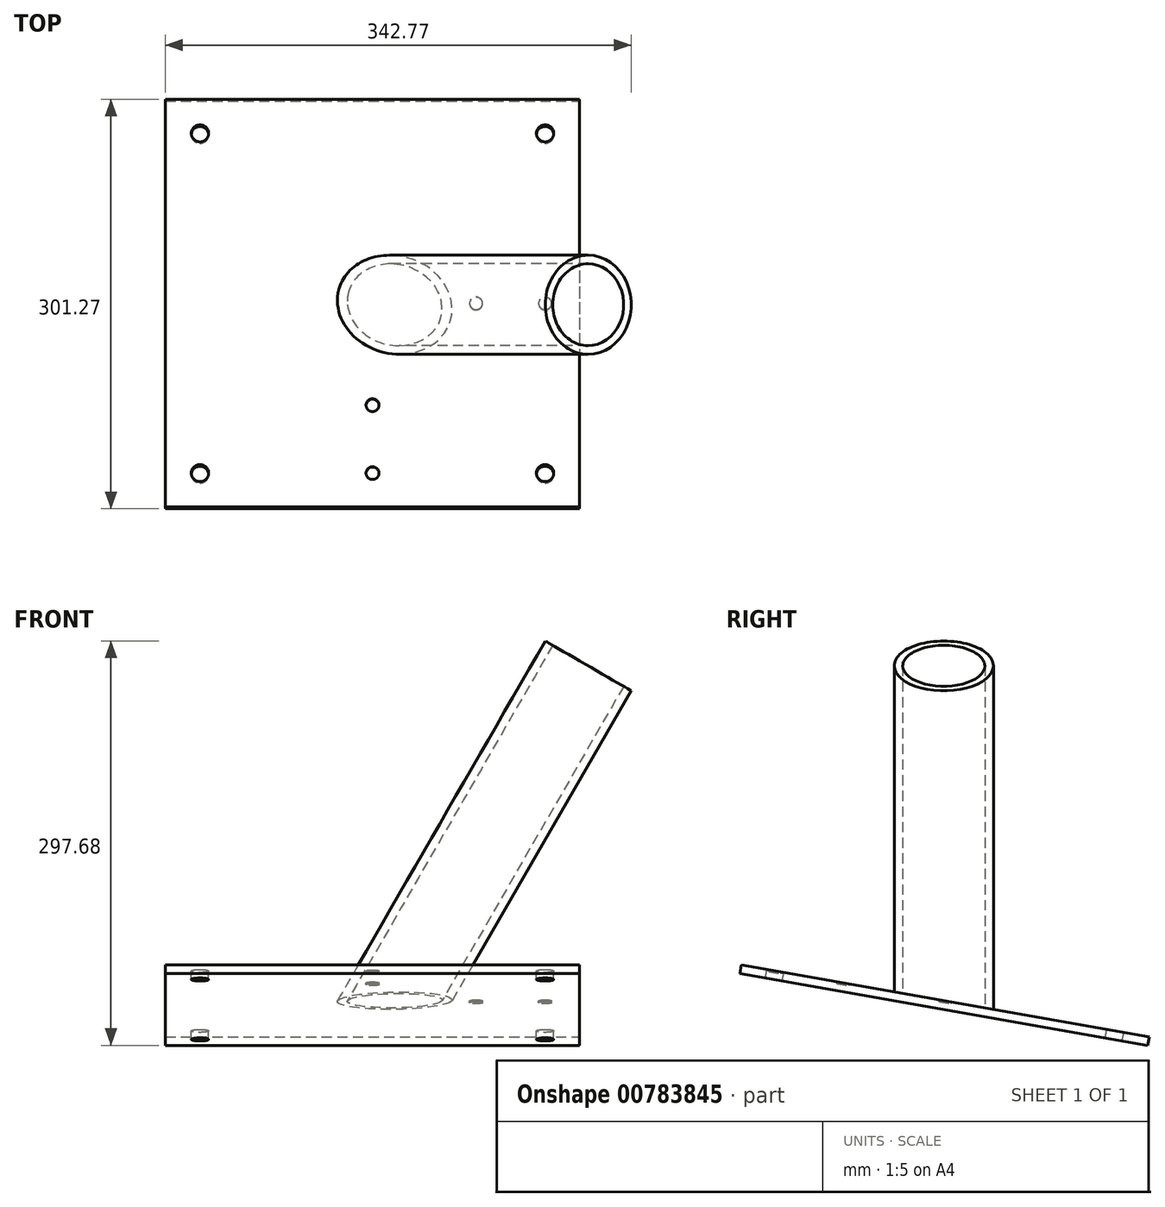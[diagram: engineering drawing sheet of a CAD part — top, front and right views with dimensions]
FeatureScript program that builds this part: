
annotation { "Feature Type Name" : "Feature", "Feature Type Description" : "" }
export const myFeature = defineFeature(function(context is Context, id is Id, definition is map)
    precondition{}
    {
        {
            var Q0;
            Q0=qCreatedBy(makeId("Top.planeOp"),FACE);
            var sketch = newSketch(context, id + "F0", { "sketchPlane" : qUnion([Q0])});
            skLineSegment(sketch, "E0.bottom", {"start": v(-25.4, 0) * mm, "end": v(0, 0) * mm});
            skLineSegment(sketch, "E0.top", {"start": v(-25.4, -25.4) * mm, "end": v(0, -25.4) * mm});
            skLineSegment(sketch, "E0.left", {"start": v(-25.4, 0) * mm, "end": v(-25.4, -25.4) * mm});
            skLineSegment(sketch, "E0.right", {"start": v(0, 0) * mm, "end": v(0, -25.4) * mm});
            skSolve(sketch);
        }
        {
            var Q0;
            Q0=sQuery(id+"F0.wireOp",EDGE,"E0.bottom");
            cPlane(context, id + "F1", {"entities" : qUnion([Q0]), "cplaneType" : CPlaneType.LINE_ANGLE, "offset" : 25.4 * mm, "angle" : 80 * degree, "width" : 152.4 * mm, "height" : 152.4 * mm});
        }
        {
            var Q0;
            Q0=qCreatedBy(id+"F1.planeOp",FACE);
            var sketch = newSketch(context, id + "F2", { "sketchPlane" : qUnion([Q0])});
            skLineSegment(sketch, "E1.bottom", {"start": v(-165.1, 152.4) * mm, "end": v(139.7, 152.4) * mm});
            skLineSegment(sketch, "E1.top", {"start": v(-165.1, -152.4) * mm, "end": v(139.7, -152.4) * mm});
            skLineSegment(sketch, "E1.left", {"start": v(-165.1, 152.4) * mm, "end": v(-165.1, -152.4) * mm});
            skLineSegment(sketch, "E1.right", {"start": v(139.7, 152.4) * mm, "end": v(139.7, -152.4) * mm});
            skSolve(sketch);
        }
        {
            var Q0;
            Q0=makeQuery(id+"F2.imprint","IMPRINT",FACE,{"disambiguationData":[TD([[makeQuery(id+"F2.imprint","IMPRINT",EDGE,{"derivedFrom":sQuery(id+"F2.wireOp",EDGE,"E1.bottom")}),-1.0]])]});
            extrude(context, id + "F3", {"entities" : qUnion([Q0]), "depth" : 6.35 * mm, "offsetDistance" : 25.4 * mm});
        }
        {
            var Q0;
            Q0=sQuery(id+"F0.wireOp",EDGE,"E0.right");
            cPlane(context, id + "F4", {"entities" : qUnion([Q0]), "cplaneType" : CPlaneType.LINE_ANGLE, "offset" : 25.4 * mm, "angle" : 330 * degree, "width" : 152.4 * mm, "height" : 152.4 * mm});
        }
        {
            var Q0;
            Q0=qCreatedBy(id+"F4.planeOp",FACE);
            var sketch = newSketch(context, id + "F5", { "sketchPlane" : qUnion([Q0])});
            skCircle(sketch, "E2", {"center": v(0, 0) * mm, "radius": 36.51 * mm});
            skCircle(sketch, "E3", {"center": v(0, 0) * mm, "radius": 30.16 * mm});
            skSolve(sketch);
        }
        {
            var Q0;
            Q0=makeQuery(id+"F5.imprint","IMPRINT",FACE,{"disambiguationData":[TD([[makeQuery(id+"F5.imprint","IMPRINT",EDGE,{"derivedFrom":sQuery(id+"F5.wireOp",EDGE,"E2")}),1.0]])]});
            extrude(context, id + "F6", {"entities" : qUnion([Q0]), "operationType" : NewBodyOperationType.ADD, "oppositeDirection" : true, "depth" : 292.1 * mm, "offsetDistance" : 25.4 * mm, "hasSecondDirection" : true, "secondDirectionOppositeDirection" : false, "secondDirectionDepth" : 15.24 * mm});
        }
        {
            var Q0;
            Q0=qCreatedBy(makeId("Right.planeOp"),FACE);
            var sketch = newSketch(context, id + "F7", { "sketchPlane" : qUnion([Q0])});
            skLineSegment(sketch, "E4", {"start": v(47.01, -8.29) * mm, "end": v(-49, 8.64) * mm});
            skLineSegment(sketch, "E5", {"start": v(-49, 8.64) * mm, "end": v(-49, -36.62) * mm});
            skLineSegment(sketch, "E6", {"start": v(-49, -36.62) * mm, "end": v(47.01, -36.62) * mm});
            skLineSegment(sketch, "E7", {"start": v(47.01, -36.62) * mm, "end": v(47.01, -8.29) * mm});
            skSolve(sketch);
        }
        {
            var Q0;
            Q0=makeQuery(id+"F7.imprint","IMPRINT",FACE,{"disambiguationData":[TD([[makeQuery(id+"F7.imprint","IMPRINT",EDGE,{"derivedFrom":sQuery(id+"F7.wireOp",EDGE,"E4")}),1.0]])]});
            extrude(context, id + "F8", {"entities" : qUnion([Q0]), "operationType" : NewBodyOperationType.REMOVE, "oppositeDirection" : true, "depth" : 50.8 * mm, "offsetDistance" : 25.4 * mm, "hasSecondDirection" : true, "secondDirectionOppositeDirection" : false, "secondDirectionDepth" : 50.8 * mm});
        }
        {
            var Q0;
            {var subQ0=sQuery(id+"F2.wireOp",EDGE,"E1.left");var subQ1=sQuery(id+"F2.wireOp",EDGE,"E1.top");var subQ2=sQuery(id+"F2.wireOp",EDGE,"E1.right");var subQ3=sQuery(id+"F2.wireOp",EDGE,"E1.bottom");Q0=makeQuery(id+"F6.boolean.opBoolean","SPLIT",FACE,{"disambiguationData":[TD([makeQuery(id+"F3.opExtrude","SWEPT_FACE",FACE,{"disambiguationData":[OSD([subQ3])]})])],"derivedFrom":makeQuery(id+"F3.opExtrude","CAP_FACE",FACE,{"disambiguationData":[OSD([subQ3,subQ1,subQ0,subQ2])],"isStart":false})});}
            var sketch = newSketch(context, id + "F9", { "sketchPlane" : qUnion([Q0])});
            skCircle(sketch, "E8", {"center": v(-12.7, -76.2) * mm, "radius": 4.76 * mm});
            skCircle(sketch, "E9", {"center": v(114.3, 0) * mm, "radius": 4.76 * mm});
            skCircle(sketch, "E10", {"center": v(63.5, 0) * mm, "radius": 4.76 * mm});
            skCircle(sketch, "E11", {"center": v(-12.7, -127) * mm, "radius": 4.76 * mm});
            skSolve(sketch);
        }
        {
            var Q0;
            Q0=makeQuery(id+"F9.imprint","IMPRINT",FACE,{"disambiguationData":[TD([[makeQuery(id+"F9.imprint","IMPRINT",EDGE,{"derivedFrom":sQuery(id+"F9.wireOp",EDGE,"E9")}),1.0]])]});
            var Q1;
            Q1=makeQuery(id+"F9.imprint","IMPRINT",FACE,{"disambiguationData":[TD([[makeQuery(id+"F9.imprint","IMPRINT",EDGE,{"derivedFrom":sQuery(id+"F9.wireOp",EDGE,"E8")}),1.0]])]});
            var Q2;
            Q2=makeQuery(id+"F9.imprint","IMPRINT",FACE,{"disambiguationData":[TD([[makeQuery(id+"F9.imprint","IMPRINT",EDGE,{"derivedFrom":sQuery(id+"F9.wireOp",EDGE,"E10")}),1.0]])]});
            var Q3;
            Q3=makeQuery(id+"F9.imprint","IMPRINT",FACE,{"disambiguationData":[TD([[makeQuery(id+"F9.imprint","IMPRINT",EDGE,{"derivedFrom":sQuery(id+"F9.wireOp",EDGE,"E11")}),1.0]])]});
            extrude(context, id + "F10", {"entities" : qUnion([Q0, Q1, Q2, Q3]), "operationType" : NewBodyOperationType.REMOVE, "oppositeDirection" : true, "depth" : 1.27 * mm, "offsetDistance" : 25.4 * mm});
        }
        {
            var Q0;
            {var subQ0=sQuery(id+"F2.wireOp",EDGE,"E1.left");var subQ1=sQuery(id+"F2.wireOp",EDGE,"E1.top");var subQ2=sQuery(id+"F2.wireOp",EDGE,"E1.right");var subQ4=sQuery(id+"F2.wireOp",EDGE,"E1.bottom");Q0=makeQuery(id+"F6.boolean.opBoolean","SPLIT",FACE,{"disambiguationData":[TD([makeQuery(id+"F3.opExtrude","SWEPT_FACE",FACE,{"disambiguationData":[OSD([subQ4])]})])],"derivedFrom":makeQuery(id+"F3.opExtrude","CAP_FACE",FACE,{"disambiguationData":[OSD([subQ4,subQ1,subQ0,subQ2])],"isStart":false})});}
            var sketch = newSketch(context, id + "F11", { "sketchPlane" : qUnion([Q0])});
            skCircle(sketch, "E12", {"center": v(-139.7, 127) * mm, "radius": 6.35 * mm});
            skCircle(sketch, "E13", {"center": v(179.57, 184.7) * mm, "radius": 7.92 * mm});
            skCircle(sketch, "E14", {"center": v(182.9, -195.52) * mm, "radius": 6.74 * mm});
            skCircle(sketch, "E15", {"center": v(-208.23, -196.87) * mm, "radius": 10.2 * mm});
            skCircle(sketch, "E16", {"center": v(114.3, 127) * mm, "radius": 6.35 * mm});
            skCircle(sketch, "E17", {"center": v(114.3, -127) * mm, "radius": 6.35 * mm});
            skCircle(sketch, "E18", {"center": v(-139.7, -127) * mm, "radius": 6.35 * mm});
            skSolve(sketch);
        }
        {
            var Q0;
            Q0=makeQuery(id+"F11.imprint","IMPRINT",FACE,{"disambiguationData":[TD([[makeQuery(id+"F11.imprint","IMPRINT",EDGE,{"derivedFrom":sQuery(id+"F11.wireOp",EDGE,"E12")}),1.0]])]});
            var Q1;
            Q1=makeQuery(id+"F11.imprint","IMPRINT",FACE,{"disambiguationData":[TD([[makeQuery(id+"F11.imprint","IMPRINT",EDGE,{"derivedFrom":sQuery(id+"F11.wireOp",EDGE,"E16")}),1.0]])]});
            var Q2;
            Q2=makeQuery(id+"F11.imprint","IMPRINT",FACE,{"disambiguationData":[TD([[makeQuery(id+"F11.imprint","IMPRINT",EDGE,{"derivedFrom":sQuery(id+"F11.wireOp",EDGE,"E17")}),1.0]])]});
            var Q3;
            Q3=makeQuery(id+"F11.imprint","IMPRINT",FACE,{"disambiguationData":[TD([[makeQuery(id+"F11.imprint","IMPRINT",EDGE,{"derivedFrom":sQuery(id+"F11.wireOp",EDGE,"E18")}),1.0]])]});
            extrude(context, id + "F12", {"entities" : qUnion([Q0, Q1, Q2, Q3]), "operationType" : NewBodyOperationType.REMOVE, "oppositeDirection" : true, "depth" : 25.4 * mm, "offsetDistance" : 25.4 * mm});
        }
    });
